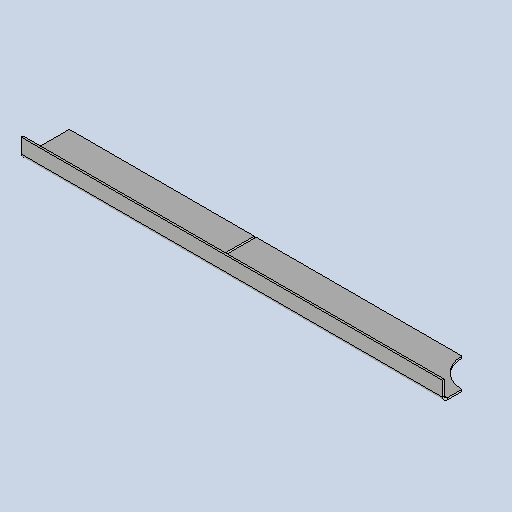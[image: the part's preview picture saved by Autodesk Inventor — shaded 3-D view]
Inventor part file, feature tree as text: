
AUTODESK INVENTOR PART (.ipt)
format: ipt  version: 2025 (Build 290162010, 162A)  size: 293,376 bytes
history: native  units: mm
features: other x5, sketch x5, sheet_metal_op x4, extrude x2
ambient origin geometry x8: Origin, YZ Plane, XZ Plane, XY Plane, X Axis, Y Axis, Z Axis, Center Point
bodies: Solid1 (feature_tree)
feature tree (16):
  sheet_metal_op  "Face1"
  sheet_metal_op  "Flange1"
  extrude  "Extrusion1"  Depth=50.0mm
  other  "Mark1"
  other  "A-Side Definition"
  extrude  "Extrusion3"  Depth=2.0mm
  sketch  "Sketch1"  dims[d0=980.0mm d1=50.0mm]
  other  "Plate1"
  sketch  "Sketch2"  dims[d2=2.0mm d3=2.0mm]
  other  "Plate2"
  sheet_metal_op  "Bend1"
  sheet_metal_op  "Corner1"
  sketch  "Sketch5"  dims[d4=1.0mm]
  sketch  "Sketch7"  dims[d5=4.0mm]
  sketch  "Sketch8"  dims[d6=2.75mm d7=20.0mm d8=90.0deg d9=2.75mm d10=8.0mm d11=2.0mm d12=2.75mm d15=0.0mm d16=0.0mm d30=12.0mm d33=60.0mm d34=2.0mm d35=31.0mm d36=490.0mm d37=0.0mm d38=0.0mm]
  other  "Definition1"
